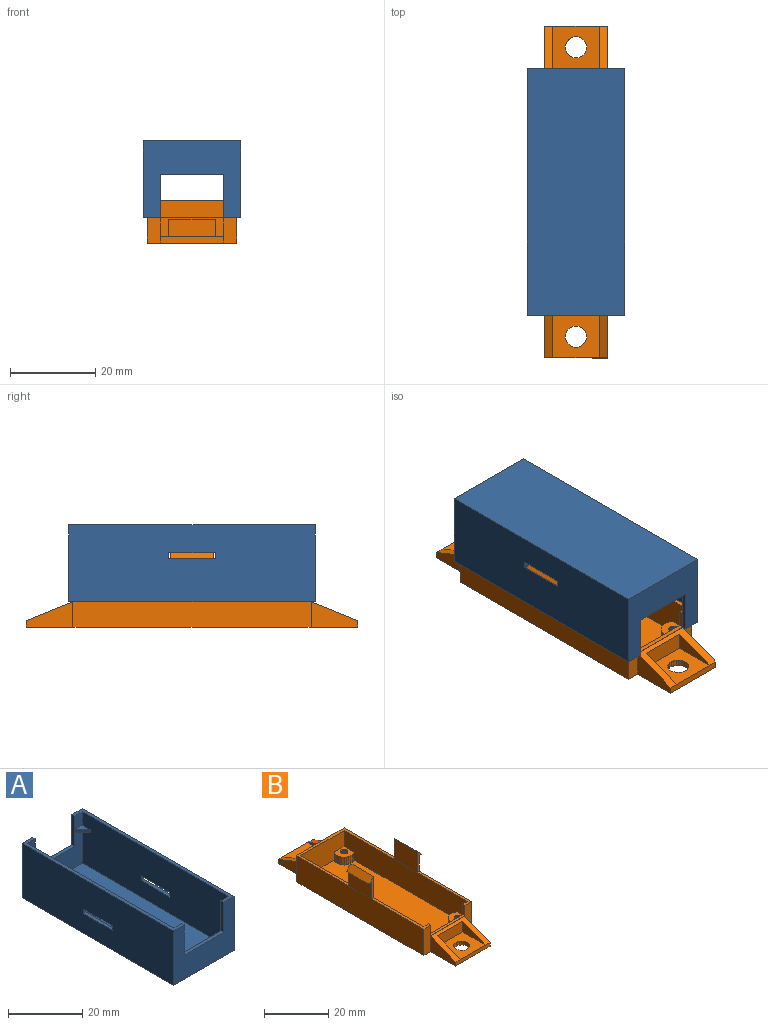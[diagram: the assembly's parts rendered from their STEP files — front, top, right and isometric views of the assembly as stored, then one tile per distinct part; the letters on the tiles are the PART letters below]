
ASSEMBLY  parts=2 mates=1
PART A: 42 faces, bbox 23x58x18 mm
  f0: plane 21x11.5mm, normal (0,-1,0), area 174mm2, adj f1,f3,f15,f24,f25,f26,f38,f41
  f1: plane 56x17mm, normal (-1,0,0), area 929.5mm2, adj f0,f2,f4,f5,f6,f15,f20,f21
  f2: plane 4.5x3mm, normal (0,-1,0), area 13.5mm2, adj f1,f6,f25,f40
  f3: plane 56x17mm, normal (1,0,0), area 929.5mm2, adj f0,f4,f7,f13,f14,f15,f16,f17
  f4: plane 21x11.5mm, normal (0,1,0), area 174mm2, adj f1,f3,f15,f27,f28,f29,f32,f35
  f5: plane 4.5x3mm, normal (0,1,0), area 13.5mm2, adj f1,f6,f28,f34
  f6: plane 58x4mm, normal (0,0,1), area 64mm2, adj f1,f2,f5,f8,f9,f10,f25,f28
  f7: plane 58x4mm, normal (0,0,1), area 64mm2, adj f3,f8,f10,f11,f13,f14,f24,f29
  f8: plane 23x18mm, normal (0,-1,0), area 264mm2, adj f6,f7,f9,f11,f12,f27,f28,f29
  f9: plane 58x18mm, normal (1,0,0), area 1027.5mm2, adj f6,f8,f10,f12,f20,f21,f22,f23
  f10: plane 23x18mm, normal (0,1,0), area 264mm2, adj f6,f7,f9,f11,f12,f24,f25,f26
  f11: plane 58x18mm, normal (-1,0,0), area 1027.5mm2, adj f7,f8,f10,f12,f16,f17,f18,f19
  f12: plane 58x23mm, normal (0,0,-1), area 1334mm2, adj f8,f9,f10,f11
  f13: plane 4.5x3mm, normal (0,1,0), area 13.5mm2, adj f3,f7,f29,f31
  f14: plane 4.5x3mm, normal (0,-1,0), area 13.5mm2, adj f3,f7,f24,f37
  f15: plane 56x21mm, normal (0,0,1), area 1176mm2, adj f0,f1,f3,f4
  f16: plane 1.5x1mm, normal (0,-1,0), area 1.5mm2, adj f3,f11,f17,f19
  f17: plane 11x1mm, normal (0,0,-1), area 11mm2, adj f3,f11,f16,f18
  f18: plane 1.5x1mm, normal (0,1,0), area 1.5mm2, adj f3,f11,f17,f19
  f19: plane 11x1mm, normal (0,0,1), area 11mm2, adj f3,f11,f16,f18
  f20: plane 11x1mm, normal (0,0,1), area 11mm2, adj f1,f9,f21,f23
  f21: plane 1.5x1mm, normal (0,1,0), area 1.5mm2, adj f1,f9,f20,f22
  f22: plane 11x1mm, normal (0,0,-1), area 11mm2, adj f1,f9,f21,f23
  f23: plane 1.5x1mm, normal (0,-1,0), area 1.5mm2, adj f1,f9,f20,f22
  f24: plane 10x1mm, normal (1,0,0), area 10mm2, adj f0,f7,f10,f14,f26,f36
  f25: plane 10x1mm, normal (-1,0,0), area 10mm2, adj f0,f2,f6,f10,f26,f39
  f26: plane 15x1mm, normal (0,0,1), area 15mm2, adj f0,f10,f24,f25
  f27: plane 15x1mm, normal (0,0,1), area 15mm2, adj f4,f8,f28,f29
  f28: plane 10x1mm, normal (-1,0,0), area 10mm2, adj f4,f5,f6,f8,f27,f33
  f29: plane 10x1mm, normal (1,0,0), area 10mm2, adj f4,f7,f8,f13,f27,f30
  f30: plane 3x3mm, normal (0.71,0.71,0), area 4.2mm2, adj f3,f29,f31,f32
  f31: plane 3x3mm, normal (0,0,1), area 4.5mm2, adj f3,f13,f30
  f32: plane 3x3mm, normal (0,0,-1), area 4.5mm2, adj f3,f4,f30
  f33: plane 3x3mm, normal (-0.71,0.71,0), area 4.2mm2, adj f1,f28,f34,f35
  f34: plane 3x3mm, normal (0,0,1), area 4.5mm2, adj f1,f5,f33
  f35: plane 3x3mm, normal (0,0,-1), area 4.5mm2, adj f1,f4,f33
  f36: plane 3x3mm, normal (0.71,-0.71,0), area 4.2mm2, adj f3,f24,f37,f38
  f37: plane 3x3mm, normal (0,0,1), area 4.5mm2, adj f3,f14,f36
  f38: plane 3x3mm, normal (0,0,-1), area 4.5mm2, adj f0,f3,f36
  f39: plane 3x3mm, normal (-0.71,-0.71,0), area 4.2mm2, adj f1,f25,f40,f41
  f40: plane 3x3mm, normal (0,0,1), area 4.5mm2, adj f1,f2,f39
  f41: plane 3x3mm, normal (0,0,-1), area 4.5mm2, adj f0,f1,f39
PART B: 250 faces, bbox 23x78x18 mm
  f0: plane 23x21mm, normal (0,0,1), area 65mm2, adj f184,f185,f193,f196,f198,f204,f240,f244
  f1: plane 23x3mm, normal (0,0,1), area 25mm2, adj f184,f195,f197,f198,f217,f242
  f2: plane 3x0.23mm, normal (-0.64,-0.77,0), area 0.9mm2, adj f4,f6,f83,f175
  f3: plane 3x0.22mm, normal (0.73,-0.68,0), area 0.9mm2, adj f5,f8,f90,f186
  f4: plane 3x0.24mm, normal (-0.81,-0.59,0), area 0.9mm2, adj f2,f10,f83,f175
  f5: plane 3x0.26mm, normal (0.88,-0.48,0), area 0.9mm2, adj f3,f12,f90,f186
  f6: plane 3x0.27mm, normal (-0.43,-0.9,0), area 0.9mm2, adj f2,f14,f83,f175
  f7: plane 3x0.25mm, normal (0.54,0.84,0), area 0.9mm2, adj f11,f15,f98,f194
  f8: plane 3x0.25mm, normal (0.54,-0.84,0), area 0.9mm2, adj f3,f16,f90,f186
  f9: plane 3x0.27mm, normal (-0.43,0.9,0), area 0.9mm2, adj f13,f17,f101,f191
  f10: plane 3x0.28mm, normal (-0.93,-0.37,0), area 0.9mm2, adj f4,f18,f83,f175
  f11: plane 3x0.29mm, normal (0.31,0.95,0), area 0.9mm2, adj f7,f19,f98,f194
  f12: plane 3x0.29mm, normal (0.97,-0.25,0), area 0.9mm2, adj f5,f20,f90,f186
  f13: plane 3x0.23mm, normal (-0.64,0.77,0), area 0.9mm2, adj f9,f21,f101,f191
  f14: plane 3x0.3mm, normal (-0.19,-0.98,0), area 0.9mm2, adj f6,f22,f83,f175
  f15: plane 3x0.22mm, normal (0.73,0.68,0), area 0.9mm2, adj f7,f23,f98,f194
  f16: plane 3x0.29mm, normal (0.31,-0.95,0), area 0.9mm2, adj f8,f24,f90,f186
  f17: plane 3x0.3mm, normal (-0.19,0.98,0), area 0.9mm2, adj f9,f25,f101,f191
  f18: plane 3x0.3mm, normal (-0.99,-0.13,0), area 0.9mm2, adj f10,f26,f83,f175
  f19: plane 3x0.3mm, normal (0.06,1,0), area 0.9mm2, adj f11,f27,f98,f194
  f20: plane 3x0.3mm, normal (1,0,0), area 0.9mm2, adj f12,f28,f90,f186
  f21: plane 3x0.24mm, normal (-0.81,0.59,0), area 0.9mm2, adj f13,f29,f101,f191
  f22: plane 3x0.3mm, normal (0.06,-1,0), area 0.9mm2, adj f14,f30,f83,f175
  f23: plane 3x0.26mm, normal (0.88,0.48,0), area 0.9mm2, adj f15,f31,f98,f194
  f24: plane 3x0.3mm, normal (0.06,-1,0), area 0.9mm2, adj f16,f32,f90,f186
  f25: plane 3x0.3mm, normal (0.06,1,0), area 0.9mm2, adj f17,f33,f101,f191
  f26: plane 3x0.3mm, normal (-0.99,0.13,0), area 0.9mm2, adj f18,f34,f83,f175
  f27: plane 3x0.3mm, normal (-0.19,0.98,0), area 0.9mm2, adj f19,f35,f98,f194
  f28: plane 3x0.29mm, normal (0.97,0.25,0), area 0.9mm2, adj f20,f36,f90,f186
  f29: plane 3x0.28mm, normal (-0.93,0.37,0), area 0.9mm2, adj f21,f37,f101,f191
  f30: plane 3x0.29mm, normal (0.31,-0.95,0), area 0.9mm2, adj f22,f38,f83,f175
  f31: plane 3x0.29mm, normal (0.97,0.25,0), area 0.9mm2, adj f23,f39,f98,f194
  f32: plane 3x0.3mm, normal (-0.19,-0.98,0), area 0.9mm2, adj f24,f40,f90,f186
  f33: plane 3x0.29mm, normal (0.31,0.95,0), area 0.9mm2, adj f25,f41,f101,f191
  f34: plane 3x0.28mm, normal (-0.93,0.37,0), area 0.9mm2, adj f26,f42,f83,f175
  f35: plane 3x0.27mm, normal (-0.43,0.9,0), area 0.9mm2, adj f27,f43,f98,f194
  f36: plane 3x0.26mm, normal (0.88,0.48,0), area 0.9mm2, adj f28,f44,f90,f186
  f37: plane 3x0.3mm, normal (-0.99,0.13,0), area 0.9mm2, adj f29,f45,f101,f191
  f38: plane 3x0.25mm, normal (0.54,-0.84,0), area 0.9mm2, adj f30,f46,f83,f175
  f39: plane 3x0.3mm, normal (1,0,0), area 0.9mm2, adj f31,f47,f98,f194
  f40: plane 3x0.27mm, normal (-0.43,-0.9,0), area 0.9mm2, adj f32,f48,f90,f186
  f41: plane 3x0.25mm, normal (0.54,0.84,0), area 0.9mm2, adj f33,f49,f101,f191
  f42: plane 3x0.24mm, normal (-0.81,0.59,0), area 0.9mm2, adj f34,f50,f83,f175
  f43: plane 3x0.23mm, normal (-0.64,0.77,0), area 0.9mm2, adj f35,f51,f98,f194
  f44: plane 3x0.22mm, normal (0.73,0.68,0), area 0.9mm2, adj f36,f52,f90,f186
  f45: plane 3x0.3mm, normal (-0.99,-0.13,0), area 0.9mm2, adj f37,f53,f101,f191
  f46: plane 3x0.22mm, normal (0.73,-0.68,0), area 0.9mm2, adj f38,f54,f83,f175
  f47: plane 3x0.29mm, normal (0.97,-0.25,0), area 0.9mm2, adj f39,f55,f98,f194
  f48: plane 3x0.23mm, normal (-0.64,-0.77,0), area 0.9mm2, adj f40,f56,f90,f186
  f49: plane 3x0.22mm, normal (0.73,0.68,0), area 0.9mm2, adj f41,f57,f101,f191
  f50: plane 3x0.23mm, normal (-0.64,0.77,0), area 0.9mm2, adj f42,f58,f83,f175
  f51: plane 3x0.24mm, normal (-0.81,0.59,0), area 0.9mm2, adj f43,f59,f98,f194
  f52: plane 3x0.25mm, normal (0.54,0.84,0), area 0.9mm2, adj f44,f60,f90,f186
  f53: plane 3x0.28mm, normal (-0.93,-0.37,0), area 0.9mm2, adj f45,f61,f101,f191
  f54: plane 3x0.26mm, normal (0.88,-0.48,0), area 0.9mm2, adj f46,f62,f83,f175
  f55: plane 3x0.26mm, normal (0.88,-0.48,0), area 0.9mm2, adj f47,f63,f98,f194
  f56: plane 3x0.24mm, normal (-0.81,-0.59,0), area 0.9mm2, adj f48,f64,f90,f186
  f57: plane 3x0.26mm, normal (0.88,0.48,0), area 0.9mm2, adj f49,f65,f101,f191
  f58: plane 3x0.27mm, normal (-0.43,0.9,0), area 0.9mm2, adj f50,f66,f83,f175
  f59: plane 3x0.28mm, normal (-0.93,0.37,0), area 0.9mm2, adj f51,f67,f98,f194
  f60: plane 3x0.29mm, normal (0.31,0.95,0), area 0.9mm2, adj f52,f68,f90,f186
  f61: plane 3x0.24mm, normal (-0.81,-0.59,0), area 0.9mm2, adj f53,f69,f101,f191
  f62: plane 3x0.29mm, normal (0.97,-0.25,0), area 0.9mm2, adj f54,f70,f83,f175
  f63: plane 3x0.22mm, normal (0.73,-0.68,0), area 0.9mm2, adj f55,f71,f98,f194
  f64: plane 3x0.28mm, normal (-0.93,-0.37,0), area 0.9mm2, adj f56,f72,f90,f186
  f65: plane 3x0.29mm, normal (0.97,0.25,0), area 0.9mm2, adj f57,f73,f101,f191
  f66: plane 3x0.3mm, normal (-0.19,0.98,0), area 0.9mm2, adj f58,f74,f83,f175
  f67: plane 3x0.3mm, normal (-0.99,0.13,0), area 0.9mm2, adj f59,f75,f98,f194
  f68: plane 3x0.3mm, normal (0.06,1,0), area 0.9mm2, adj f60,f76,f90,f186
  f69: plane 3x0.23mm, normal (-0.64,-0.77,0), area 0.9mm2, adj f61,f77,f101,f191
  f70: plane 3x0.3mm, normal (1,0,0), area 0.9mm2, adj f62,f78,f83,f175
  f71: plane 3x0.25mm, normal (0.54,-0.84,0), area 0.9mm2, adj f63,f79,f98,f194
  f72: plane 3x0.3mm, normal (-0.99,-0.13,0), area 0.9mm2, adj f64,f80,f90,f186
  f73: plane 3x0.3mm, normal (1,0,0), area 0.9mm2, adj f65,f81,f101,f191
  f74: plane 3x0.3mm, normal (0.06,1,0), area 0.9mm2, adj f66,f82,f83,f175
  f75: plane 3x0.3mm, normal (-0.99,-0.13,0), area 0.9mm2, adj f67,f84,f98,f194
  f76: plane 3x0.3mm, normal (-0.19,0.98,0), area 0.9mm2, adj f68,f85,f90,f186
  f77: plane 3x0.27mm, normal (-0.43,-0.9,0), area 0.9mm2, adj f69,f86,f101,f191
  f78: plane 3x0.29mm, normal (0.97,0.25,0), area 0.9mm2, adj f70,f83,f87,f175
  f79: plane 3x0.29mm, normal (0.31,-0.95,0), area 0.9mm2, adj f71,f88,f98,f194
  f80: plane 3x0.3mm, normal (-0.99,0.13,0), area 0.9mm2, adj f72,f89,f90,f186
  f81: plane 3x0.29mm, normal (0.97,-0.25,0), area 0.9mm2, adj f73,f91,f101,f191
  f82: plane 3x0.29mm, normal (0.31,0.95,0), area 0.9mm2, adj f74,f83,f92,f175
  f83: plane 2.4x2.39mm, normal (0,0,1), area 4.5mm2, adj f2,f4,f6,f10,f14,f18,f22,f26
  f84: plane 3x0.28mm, normal (-0.93,-0.37,0), area 0.9mm2, adj f75,f93,f98,f194
  f85: plane 3x0.27mm, normal (-0.43,0.9,0), area 0.9mm2, adj f76,f90,f94,f186
  f86: plane 3x0.3mm, normal (-0.19,-0.98,0), area 0.9mm2, adj f77,f95,f101,f191
  f87: plane 3x0.26mm, normal (0.88,0.48,0), area 0.9mm2, adj f78,f83,f96,f175
  f88: plane 3x0.3mm, normal (0.06,-1,0), area 0.9mm2, adj f79,f97,f98,f194
  f89: plane 3x0.28mm, normal (-0.93,0.37,0), area 0.9mm2, adj f80,f90,f99,f186
  f90: plane 2.4x2.39mm, normal (0,0,1), area 4.5mm2, adj f3,f5,f8,f12,f16,f20,f24,f28
  f91: plane 3x0.26mm, normal (0.88,-0.48,0), area 0.9mm2, adj f81,f100,f101,f191
  f92: plane 3x0.25mm, normal (0.54,0.84,0), area 0.9mm2, adj f82,f83,f96,f175
  f93: plane 3x0.24mm, normal (-0.81,-0.59,0), area 0.9mm2, adj f84,f98,f102,f194
  f94: plane 3x0.23mm, normal (-0.64,0.77,0), area 0.9mm2, adj f85,f90,f99,f186
  f95: plane 3x0.3mm, normal (0.06,-1,0), area 0.9mm2, adj f86,f101,f104,f191
  f96: plane 3x0.22mm, normal (0.73,0.68,0), area 0.9mm2, adj f83,f87,f92,f175
  f97: plane 3x0.3mm, normal (-0.19,-0.98,0), area 0.9mm2, adj f88,f98,f105,f194
  f98: plane 2.4x2.39mm, normal (0,0,1), area 4.5mm2, adj f7,f11,f15,f19,f23,f27,f31,f35
  f99: plane 3x0.24mm, normal (-0.81,0.59,0), area 0.9mm2, adj f89,f90,f94,f186
  f100: plane 3x0.22mm, normal (0.73,-0.68,0), area 0.9mm2, adj f91,f101,f107,f191
  f101: plane 2.4x2.39mm, normal (0,0,1), area 4.5mm2, adj f9,f13,f17,f21,f25,f29,f33,f37
  f102: plane 3x0.23mm, normal (-0.64,-0.77,0), area 0.9mm2, adj f93,f98,f105,f194
  f103: plane 3x0.6mm, normal (-0.79,-0.61,0), area 2.3mm2, adj f108,f110,f175,f188
  f104: plane 3x0.29mm, normal (0.31,-0.95,0), area 0.9mm2, adj f95,f101,f107,f191
  f105: plane 3x0.27mm, normal (-0.43,-0.9,0), area 0.9mm2, adj f97,f98,f102,f194
  f106: plane 3x0.71mm, normal (0.93,-0.37,0), area 2.3mm2, adj f109,f112,f186,f188
  f107: plane 3x0.25mm, normal (0.54,-0.84,0), area 0.9mm2, adj f100,f101,f104,f191
  f108: plane 3x0.6mm, normal (-0.61,-0.79,0), area 2.3mm2, adj f103,f114,f175,f188
  f109: plane 3x0.61mm, normal (0.8,-0.6,0), area 2.3mm2, adj f106,f115,f186,f188
  f110: plane 3x0.69mm, normal (-0.92,-0.4,0), area 2.3mm2, adj f103,f116,f175,f188
  f111: plane 3x0.69mm, normal (-0.4,0.92,0), area 2.3mm2, adj f119,f120,f188,f191
  f112: plane 3x0.76mm, normal (0.99,-0.13,0), area 2.3mm2, adj f106,f122,f186,f188
  f113: plane 3x0.6mm, normal (0.63,0.78,0), area 2.3mm2, adj f121,f124,f188,f194
  f114: plane 3x0.69mm, normal (-0.4,-0.92,0), area 2.3mm2, adj f108,f125,f175,f188
  f115: plane 3x0.6mm, normal (0.63,-0.78,0), area 2.3mm2, adj f109,f126,f186,f188
  f116: plane 3x0.75mm, normal (-0.99,-0.15,0), area 2.3mm2, adj f110,f127,f175,f188
  f117: plane 1.5x0.6mm, normal (-0.31,-0.95,0), area 0.9mm2, adj f118,f123,f173,f211
  f118: plane 1.5x0.63mm, normal (-0.06,-1,0), area 0.9mm2, adj f117,f129,f173,f211
  f119: plane 3x0.6mm, normal (-0.61,0.79,0), area 2.3mm2, adj f111,f130,f188,f191
  f120: plane 3x0.75mm, normal (-0.15,0.99,0), area 2.3mm2, adj f111,f131,f188,f191
  f121: plane 3x0.7mm, normal (0.41,0.91,0), area 2.3mm2, adj f113,f132,f188,f194
  f122: plane 3x0.72mm, normal (0.99,0.12,0), area 2.2mm2, adj f112,f133,f186,f188
  f123: plane 1.5x0.53mm, normal (-0.54,-0.84,0), area 0.9mm2, adj f117,f128,f173,f211
  f124: plane 3x0.61mm, normal (0.8,0.6,0), area 2.3mm2, adj f113,f137,f188,f194
  f125: plane 3x0.75mm, normal (-0.15,-0.99,0), area 2.3mm2, adj f114,f138,f175,f188
  f126: plane 3x0.7mm, normal (0.41,-0.91,0), area 2.3mm2, adj f115,f139,f186,f188
  f127: plane 3x0.75mm, normal (-1,0.1,0), area 2.3mm2, adj f116,f140,f175,f188
  f128: plane 1.5x0.46mm, normal (-0.73,-0.68,0), area 0.9mm2, adj f123,f134,f173,f211
  f129: plane 1.5x0.62mm, normal (0.19,-0.98,0), area 0.9mm2, adj f118,f136,f173,f211
  f130: plane 3x0.6mm, normal (-0.79,0.61,0), area 2.3mm2, adj f119,f146,f188,f191
  f131: plane 3x0.75mm, normal (0.1,1,0), area 2.3mm2, adj f120,f147,f188,f191
  f132: plane 3x0.75mm, normal (0.16,0.99,0), area 2.3mm2, adj f121,f148,f188,f194
  f133: plane 3x0.68mm, normal (0.93,0.36,0), area 2.2mm2, adj f122,f149,f186,f188
  f134: plane 1.5x0.55mm, normal (-0.88,-0.48,0), area 0.9mm2, adj f128,f142,f173,f211
  f135: plane 1.5x0.46mm, normal (-0.73,0.68,0), area 0.9mm2, adj f141,f143,f173,f211
  f136: plane 1.5x0.57mm, normal (0.43,-0.9,0), area 0.9mm2, adj f129,f144,f173,f211
  f137: plane 3x0.71mm, normal (0.93,0.37,0), area 2.3mm2, adj f124,f156,f188,f194
  f138: plane 3x0.75mm, normal (0.1,-1,0), area 2.3mm2, adj f125,f157,f175,f188
  f139: plane 3x0.75mm, normal (0.16,-0.99,0), area 2.3mm2, adj f126,f158,f186,f188
  f140: plane 3x0.71mm, normal (-0.94,0.34,0), area 2.3mm2, adj f127,f159,f175,f188
  f141: plane 1.5x0.55mm, normal (-0.88,0.48,0), area 0.9mm2, adj f135,f150,f173,f211
  f142: plane 1.5x0.61mm, normal (-0.97,-0.25,0), area 0.9mm2, adj f134,f151,f173,f211
  f143: plane 1.5x0.53mm, normal (-0.54,0.84,0), area 0.9mm2, adj f135,f153,f173,f211
  f144: plane 1.5x0.48mm, normal (0.64,-0.77,0), area 0.9mm2, adj f136,f154,f173,f211
  f145: plane 1.5x0.48mm, normal (0.64,0.77,0), area 0.9mm2, adj f152,f155,f173,f211
  f146: plane 3x0.69mm, normal (-0.92,0.4,0), area 2.3mm2, adj f130,f164,f188,f191
  f147: plane 3x0.71mm, normal (0.34,0.94,0), area 2.3mm2, adj f131,f165,f188,f191
  f148: plane 3x0.76mm, normal (-0.09,1,0), area 2.3mm2, adj f132,f166,f188,f194
  f149: plane 3x0.6mm, normal (0.82,0.57,0), area 2.2mm2, adj f133,f185,f186,f188
  f150: plane 1.5x0.61mm, normal (-0.97,0.25,0), area 0.9mm2, adj f141,f151,f173,f211
  f151: plane 1.5x0.63mm, normal (-1,0,0), area 0.9mm2, adj f142,f150,f173,f211
  f152: plane 1.5x0.57mm, normal (0.43,0.9,0), area 0.9mm2, adj f145,f160,f173,f211
  f153: plane 1.5x0.6mm, normal (-0.31,0.95,0), area 0.9mm2, adj f143,f161,f173,f211
  f154: plane 1.5x0.51mm, normal (0.81,-0.59,0), area 0.9mm2, adj f144,f162,f173,f211
  f155: plane 1.5x0.51mm, normal (0.81,0.59,0), area 0.9mm2, adj f145,f163,f173,f211
  f156: plane 3x0.76mm, normal (0.99,0.13,0), area 2.3mm2, adj f137,f169,f188,f194
  f157: plane 3x0.71mm, normal (0.34,-0.94,0), area 2.3mm2, adj f138,f170,f175,f188
  f158: plane 3x0.76mm, normal (-0.09,-1,0), area 2.3mm2, adj f139,f171,f186,f188
  f159: plane 3x0.62mm, normal (-0.82,0.57,0), area 2.3mm2, adj f140,f175,f185,f188
  f160: plane 1.5x0.62mm, normal (0.19,0.98,0), area 0.9mm2, adj f152,f161,f173,f211
  f161: plane 1.5x0.63mm, normal (-0.06,1,0), area 0.9mm2, adj f153,f160,f173,f211
  f162: plane 1.5x0.58mm, normal (0.93,-0.37,0), area 0.9mm2, adj f154,f167,f173,f211
  f163: plane 1.5x0.58mm, normal (0.93,0.37,0), area 0.9mm2, adj f155,f168,f173,f211
  f164: plane 3x0.75mm, normal (-0.99,0.15,0), area 2.3mm2, adj f146,f174,f188,f191
  f165: plane 3x0.62mm, normal (0.57,0.82,0), area 2.3mm2, adj f147,f184,f188,f191
  f166: plane 3x0.72mm, normal (-0.34,0.94,0), area 2.3mm2, adj f148,f177,f188,f194
  f167: plane 1.5x0.62mm, normal (0.99,-0.13,0), area 0.9mm2, adj f162,f168,f173,f211
  f168: plane 1.5x0.62mm, normal (0.99,0.13,0), area 0.9mm2, adj f163,f167,f173,f211
  f169: plane 3x0.72mm, normal (0.99,-0.12,0), area 2.2mm2, adj f156,f180,f188,f194
  f170: plane 3x0.62mm, normal (0.57,-0.82,0), area 2.3mm2, adj f157,f175,f184,f188
  f171: plane 3x0.72mm, normal (-0.34,-0.94,0), area 2.3mm2, adj f158,f181,f186,f188
  f172: plane 10x4.04mm, normal (-1,0,0), area 20.2mm2, adj f173,f182,f190
  f173: plane 11x10mm, normal (0,0,1), area 90.6mm2, adj f117,f118,f123,f128,f129,f134,f135,f136
  f174: plane 3x0.75mm, normal (-1,-0.1,0), area 2.3mm2, adj f164,f183,f188,f191
  f175: plane 5x5mm, normal (0,0,1), area 17.5mm2, adj f2,f4,f6,f10,f14,f18,f22,f26
  f176: plane 11x5.94mm, normal (1,0,0), area 40.9mm2, adj f179,f190,f196,f211
  f177: plane 3x0.63mm, normal (-0.57,0.82,0), area 2.3mm2, adj f166,f188,f193,f194
  f178: plane 10x4.04mm, normal (1,0,0), area 20.2mm2, adj f173,f182,f190
  f179: plane 15x1.5mm, normal (0,1,0), area 22.5mm2, adj f173,f176,f187,f190,f211
  f180: plane 3x0.68mm, normal (0.93,-0.36,0), area 2.2mm2, adj f169,f188,f189,f194
  f181: plane 3x0.63mm, normal (-0.57,-0.82,0), area 2.3mm2, adj f171,f186,f188,f193
  f182: plane 11x4.04mm, normal (0,1,0), area 44.4mm2, adj f172,f173,f178,f190
  f183: plane 3x0.71mm, normal (-0.94,-0.34,0), area 2.3mm2, adj f174,f188,f191,f192
  f184: plane 54x9mm, normal (-1,0,0), area 460.6mm2, adj f0,f1,f165,f170,f175,f185,f188,f191
  f185: plane 19x9mm, normal (0,-1,0), area 145.6mm2, adj f0,f149,f159,f175,f184,f186,f188,f193
  f186: plane 5x5mm, normal (0,0,1), area 17.5mm2, adj f3,f5,f8,f12,f16,f20,f24,f28
  f187: plane 11x5.94mm, normal (-1,0,0), area 40.9mm2, adj f179,f190,f196,f211
  f188: plane 54x19mm, normal (0,0,1), area 938.1mm2, adj f103,f106,f108,f109,f110,f111,f112,f113
  f189: plane 3x0.6mm, normal (0.82,-0.57,0), area 2.2mm2, adj f180,f188,f194,f197
  f190: plane 15x11mm, normal (0,0.37,0.93), area 59.3mm2, adj f172,f176,f178,f179,f182,f187,f196
  f191: plane 5x5mm, normal (0,0,1), area 17.5mm2, adj f9,f13,f17,f21,f25,f29,f33,f37
  f192: plane 3x0.62mm, normal (-0.82,-0.57,0), area 2.3mm2, adj f183,f188,f191,f197
  f193: plane 54x9mm, normal (1,0,0), area 460.6mm2, adj f0,f177,f181,f185,f186,f188,f194,f197
  f194: plane 5x5mm, normal (0,0,1), area 17.5mm2, adj f7,f11,f15,f19,f23,f27,f31,f35
  f195: plane 4x1mm, normal (-1,0,0), area 4mm2, adj f1,f197,f206,f217
  f196: plane 21x10mm, normal (0,1,0), area 120.8mm2, adj f0,f176,f187,f190,f198,f204,f211
  f197: plane 19x9mm, normal (0,1,0), area 85.6mm2, adj f1,f184,f188,f189,f191,f192,f193,f194
  f198: plane 56x10mm, normal (1,0,0), area 560mm2, adj f0,f1,f196,f211,f217,f243
  f199: plane 23x3mm, normal (0,0,1), area 25mm2, adj f193,f197,f200,f204,f217,f238
  f200: plane 4x1mm, normal (1,0,0), area 4mm2, adj f197,f199,f206,f217
  f201: plane 1.5x0.57mm, normal (-0.43,0.9,0), area 0.9mm2, adj f202,f203,f211,f237
  f202: plane 1.5x0.48mm, normal (-0.64,0.77,0), area 0.9mm2, adj f201,f205,f211,f237
  f203: plane 1.5x0.62mm, normal (-0.19,0.98,0), area 0.9mm2, adj f201,f210,f211,f237
  f204: plane 56x10mm, normal (-1,0,0), area 560mm2, adj f0,f196,f199,f211,f217,f241
  f205: plane 1.5x0.51mm, normal (-0.81,0.59,0), area 0.9mm2, adj f202,f208,f211,f237
  f206: plane 15x1mm, normal (0,0,1), area 15mm2, adj f195,f197,f200,f217
  f207: plane 1.5x0.58mm, normal (-0.93,-0.37,0), area 0.9mm2, adj f209,f211,f213,f237
  f208: plane 1.5x0.58mm, normal (-0.93,0.37,0), area 0.9mm2, adj f205,f211,f214,f237
  f209: plane 1.5x0.51mm, normal (-0.81,-0.59,0), area 0.9mm2, adj f207,f211,f215,f237
  f210: plane 1.5x0.63mm, normal (0.06,1,0), area 0.9mm2, adj f203,f211,f216,f237
  f211: plane 78x21mm, normal (0,0,-1), area 1467.1mm2, adj f117,f118,f123,f128,f129,f134,f135,f136
  f212: plane 11x5.94mm, normal (1,0,0), area 40.9mm2, adj f211,f217,f226,f229
  f213: plane 1.5x0.62mm, normal (-0.99,-0.13,0), area 0.9mm2, adj f207,f211,f214,f237
  f214: plane 1.5x0.62mm, normal (-0.99,0.13,0), area 0.9mm2, adj f208,f211,f213,f237
  f215: plane 1.5x0.48mm, normal (-0.64,-0.77,0), area 0.9mm2, adj f209,f211,f218,f237
  f216: plane 1.5x0.6mm, normal (0.31,0.95,0), area 0.9mm2, adj f210,f211,f219,f237
  f217: plane 21x10mm, normal (0,-1,0), area 60.8mm2, adj f1,f195,f198,f199,f200,f204,f206,f211
  f218: plane 1.5x0.57mm, normal (-0.43,-0.9,0), area 0.9mm2, adj f211,f215,f221,f237
  f219: plane 1.5x0.53mm, normal (0.54,0.84,0), area 0.9mm2, adj f211,f216,f220,f237
  f220: plane 1.5x0.46mm, normal (0.73,0.68,0), area 0.9mm2, adj f211,f219,f224,f237
  f221: plane 1.5x0.62mm, normal (-0.19,-0.98,0), area 0.9mm2, adj f211,f218,f225,f237
  f222: plane 11x5.94mm, normal (-1,0,0), area 40.9mm2, adj f211,f217,f226,f229
  f223: plane 10x4.04mm, normal (-1,0,0), area 20.2mm2, adj f229,f230,f237
  f224: plane 1.5x0.55mm, normal (0.88,0.48,0), area 0.9mm2, adj f211,f220,f227,f237
  f225: plane 1.5x0.63mm, normal (0.06,-1,0), area 0.9mm2, adj f211,f221,f228,f237
  f226: plane 15x1.5mm, normal (0,-1,0), area 22.5mm2, adj f211,f212,f222,f229,f237
  f227: plane 1.5x0.61mm, normal (0.97,0.25,0), area 0.9mm2, adj f211,f224,f231,f237
  f228: plane 1.5x0.6mm, normal (0.31,-0.95,0), area 0.9mm2, adj f211,f225,f232,f237
  f229: plane 15x11mm, normal (0,-0.37,0.93), area 59.3mm2, adj f212,f217,f222,f223,f226,f230,f233
  f230: plane 11x4.04mm, normal (0,-1,0), area 44.4mm2, adj f223,f229,f233,f237
  f231: plane 1.5x0.63mm, normal (1,0,0), area 0.9mm2, adj f211,f227,f234,f237
  f232: plane 1.5x0.53mm, normal (0.54,-0.84,0), area 0.9mm2, adj f211,f228,f235,f237
  f233: plane 10x4.04mm, normal (1,0,0), area 20.2mm2, adj f229,f230,f237
  f234: plane 1.5x0.61mm, normal (0.97,-0.25,0), area 0.9mm2, adj f211,f231,f236,f237
  f235: plane 1.5x0.46mm, normal (0.73,-0.68,0), area 0.9mm2, adj f211,f232,f236,f237
  f236: plane 1.5x0.55mm, normal (0.88,-0.48,0), area 0.9mm2, adj f211,f234,f235,f237
  f237: plane 11x10mm, normal (0,0,1), area 90.6mm2, adj f201,f202,f203,f205,f207,f208,f209,f210
  f238: plane 8x2mm, normal (0,-1,0), area 8mm2, adj f199,f239,f241,f246,f247
  f239: bspline ~10x8mm, area 80mm2, adj f193,f238,f240,f247
  f240: plane 8x2mm, normal (0,1,0), area 8mm2, adj f0,f239,f241,f246,f247
  f241: bspline ~10x8mm, area 60mm2, adj f204,f238,f240,f246
  f242: plane 8x2mm, normal (0,-1,0), area 8mm2, adj f1,f243,f245,f248,f249
  f243: bspline ~10x8mm, area 60mm2, adj f198,f242,f244,f248
  f244: plane 8x2mm, normal (0,1,0), area 8mm2, adj f0,f243,f245,f248,f249
  f245: bspline ~10x8mm, area 80mm2, adj f184,f242,f244,f249
  f246: plane 10x1mm, normal (0,0,-1), area 10mm2, adj f238,f240,f241,f247
  f247: plane 10x2mm, normal (-0.71,0,0.71), area 28.3mm2, adj f238,f239,f240,f246
  f248: plane 10x1mm, normal (0,0,-1), area 10mm2, adj f242,f243,f244,f249
  f249: plane 10x2mm, normal (0.71,0,0.71), area 28.3mm2, adj f242,f244,f245,f248
PLACE A rot(axis=(1,0,0),180deg) t=(9.5,27,24)mm
PLACE B at identity
MATE fastened A.f22 <-> B.f248  axis (0,0,1) through (20.5,27,16)mm
